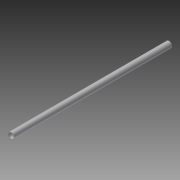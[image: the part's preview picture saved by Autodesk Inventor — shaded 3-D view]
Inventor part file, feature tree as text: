
AUTODESK INVENTOR PART (.ipt)
format: ipt  version: 2013 (Build 170138000, 138)  size: 68,096 bytes
history: native  units: in
note: dims shown in document units (in); Inventor stores cm internally (conversion verified against a paired STEP export)
features: extrude x1, sketch x1
ambient origin geometry x8: Origin, YZ Plane, XZ Plane, XY Plane, X Axis, Y Axis, Z Axis, Center Point
bodies: Solid1 (feature_tree)
feature tree (2):
  extrude  "Extrusion1"  Depth=1.37in
  sketch  "Sketch1"  dims[d0=1.5in d2=1.37in d3=38.5in d4=0.0in]
